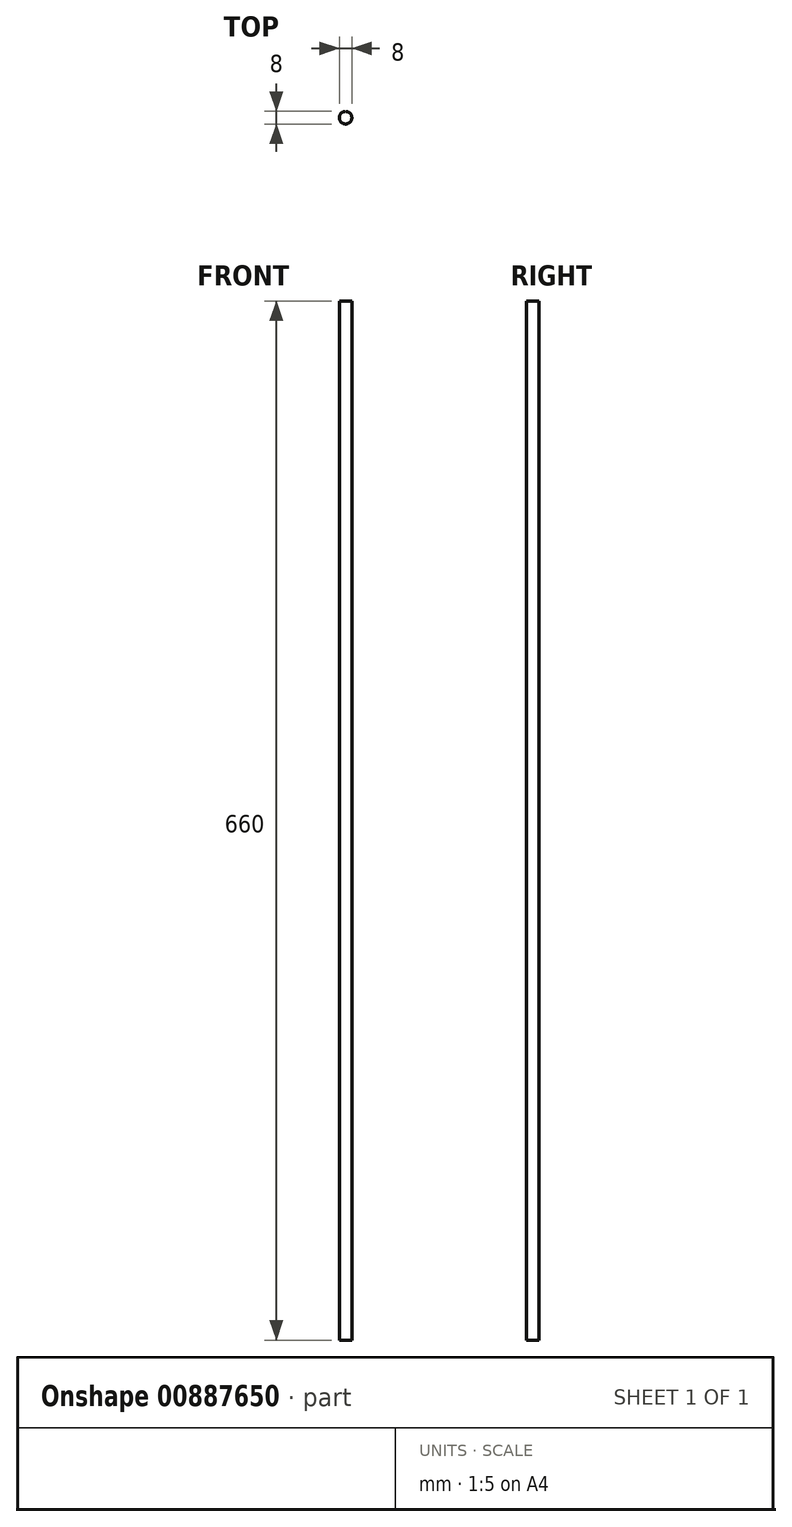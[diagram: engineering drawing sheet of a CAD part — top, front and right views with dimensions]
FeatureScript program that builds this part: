
annotation { "Feature Type Name" : "Feature", "Feature Type Description" : "" }
export const myFeature = defineFeature(function(context is Context, id is Id, definition is map)
    precondition{}
    {
        {
            var Q0;
            Q0=qCreatedBy(makeId("Top.planeOp"),FACE);
            var sketch = newSketch(context, id + "F0", { "sketchPlane" : qUnion([Q0])});
            skCircle(sketch, "E0", {"center": v(0, 0) * mm, "radius": 4 * mm});
            skSolve(sketch);
        }
        {
            var Q0;
            Q0=qSketchRegion(id+"F0",true);
            extrude(context, id + "F1", {"entities" : qUnion([Q0]), "depth" : 660 * mm});
        }
    });
